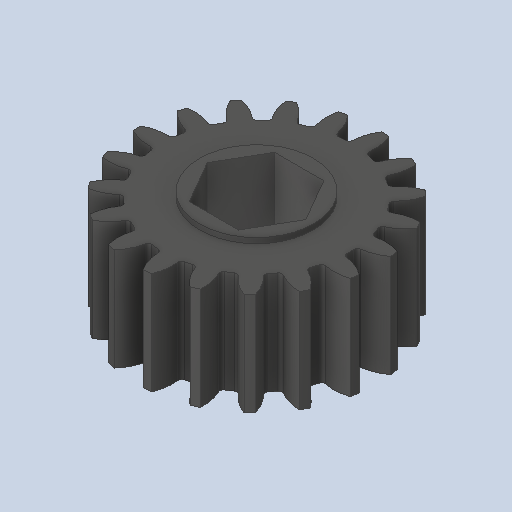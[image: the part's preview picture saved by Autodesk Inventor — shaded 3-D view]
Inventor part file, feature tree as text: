
AUTODESK INVENTOR PART (.ipt)
format: ipt  version: 2023 (Build 270158000, 158)  size: 237,568 bytes
history: native  units: in
note: dims shown in document units (in); Inventor stores cm internally (conversion verified against a paired STEP export)
features: fillet x1
ambient origin geometry x8: Origin, YZ Plane, XZ Plane, XY Plane, X Axis, Y Axis, Z Axis, Center Point
bodies: Solid1 (feature_tree)
feature tree (1):
  fillet  "Fillet1"  [1 undecoded]
note: 1 required parameter value undecoded (feature->parameter linkage not recoverable at this tier; creation-order binding heuristic only, values carry confidence <= 0.55)
